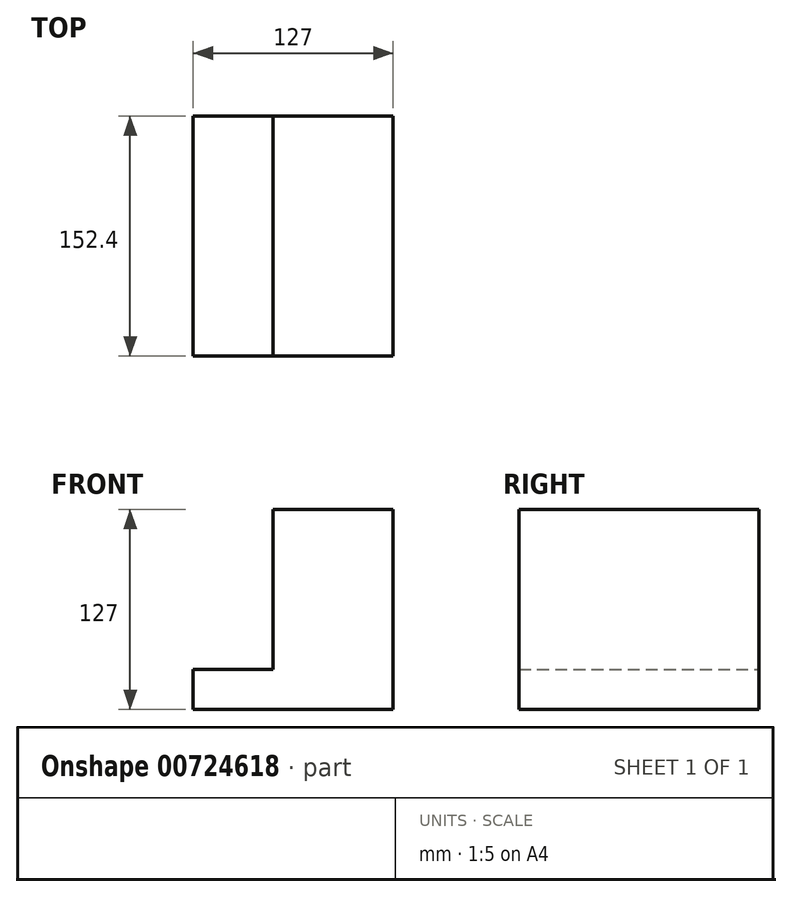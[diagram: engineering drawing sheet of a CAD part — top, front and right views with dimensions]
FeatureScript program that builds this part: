
annotation { "Feature Type Name" : "Feature", "Feature Type Description" : "" }
export const myFeature = defineFeature(function(context is Context, id is Id, definition is map)
    precondition{}
    {
        {
            var Q0;
            Q0=qCreatedBy(makeId("Front.planeOp"),FACE);
            var sketch = newSketch(context, id + "F0", { "sketchPlane" : qUnion([Q0])});
            skLineSegment(sketch, "E0", {"start": v(-75.58, -75.89) * mm, "end": v(51.42, -75.89) * mm});
            skLineSegment(sketch, "E1", {"start": v(51.42, -75.89) * mm, "end": v(51.42, 51.11) * mm});
            skLineSegment(sketch, "E2", {"start": v(51.42, 51.11) * mm, "end": v(-24.78, 51.11) * mm});
            skLineSegment(sketch, "E3", {"start": v(-24.78, 51.11) * mm, "end": v(-24.78, -50.49) * mm});
            skLineSegment(sketch, "E4", {"start": v(-24.78, -50.49) * mm, "end": v(-75.58, -50.49) * mm});
            skLineSegment(sketch, "E5", {"start": v(-75.58, -50.49) * mm, "end": v(-75.58, -75.89) * mm});
            skSolve(sketch);
        }
        {
            var Q0;
            Q0 = qSketchRegion(id + "F0", true);
            extrude(context, id + "F1", {"entities" : qUnion([Q0]), "depth" : 152.4 * mm, "offsetDistance" : 25.4 * mm});
        }
    });
